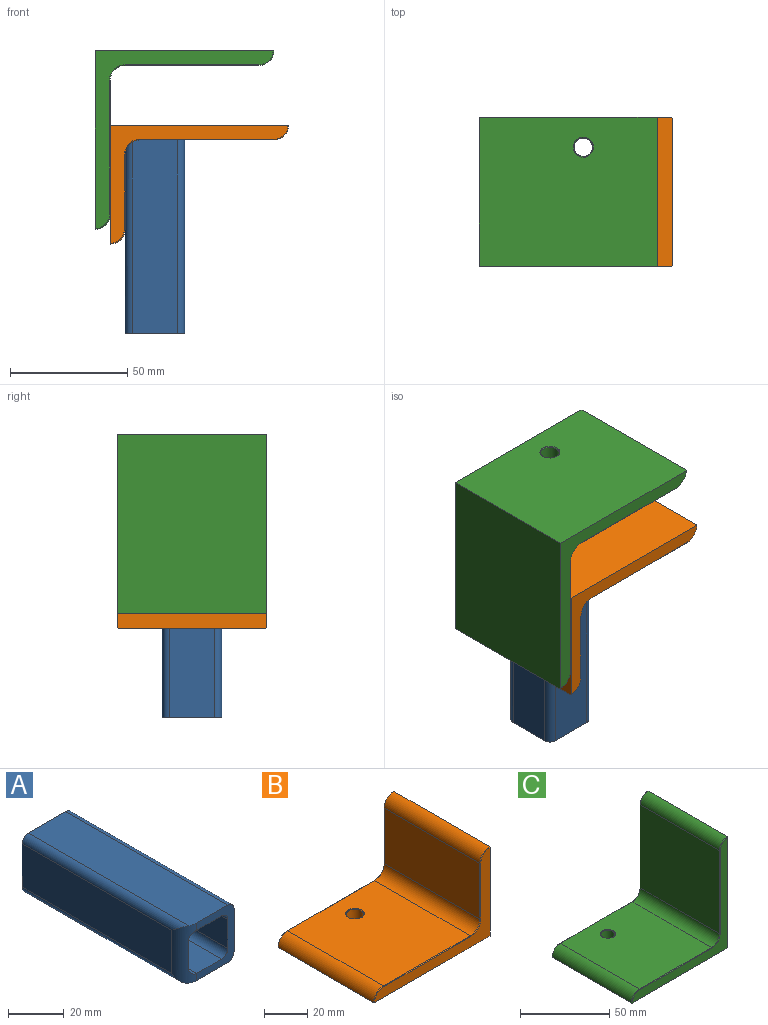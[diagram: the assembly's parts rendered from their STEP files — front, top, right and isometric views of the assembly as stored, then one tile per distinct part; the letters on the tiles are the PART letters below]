
ASSEMBLY  parts=3 mates=2
PART A: 19 faces, bbox 25.4x82.6x25.4 mm
  f0: cylinder r=3.17mm len=82.55mm, axis (0,1,0), area 411.7mm2, adj f1,f15,f16,f17
  f1: plane 82.55x12.7mm, normal (0,0,1), area 1048.4mm2, adj f0,f2,f16,f17
  f2: cylinder r=3.17mm len=82.55mm, axis (0,1,0), area 409.6mm2, adj f1,f3,f17,f18
  f3: plane 81.7x12.7mm, normal (1,0,0), area 1037.6mm2, adj f2,f4,f17,f18
  f4: cylinder r=3.17mm len=82.55mm, axis (0,1,0), area 409.6mm2, adj f3,f5,f17,f18
  f5: plane 82.55x12.7mm, normal (0,0,-1), area 1048.4mm2, adj f4,f6,f16,f17
  f6: cylinder r=3.17mm len=82.55mm, axis (0,1,0), area 411.7mm2, adj f5,f15,f16,f17
  f7: plane 82.55x19.05mm, normal (0,0,-1), area 1571.7mm2, adj f8,f14,f16,f17,f18
  f8: cylinder r=3.17mm len=82.55mm, axis (0,1,0), area 411.7mm2, adj f7,f9,f16,f17
  f9: plane 82.55x19.05mm, normal (1,0,0), area 1572.6mm2, adj f8,f10,f16,f17
  f10: cylinder r=3.17mm len=82.55mm, axis (0,1,0), area 411.7mm2, adj f9,f11,f16,f17
  f11: plane 82.55x19.05mm, normal (0,0,1), area 1571.7mm2, adj f10,f12,f16,f17,f18
  f12: cylinder r=3.17mm len=81.7mm, axis (0,1,0), area 395.6mm2, adj f11,f13,f17,f18
  f13: plane 76.2x19.05mm, normal (-1,0,0), area 1451.6mm2, adj f12,f14,f17,f18
  f14: cylinder r=3.17mm len=81.7mm, axis (0,1,0), area 395.6mm2, adj f7,f13,f17,f18
  f15: plane 82.55x12.7mm, normal (-1,0,0), area 1048.4mm2, adj f0,f6,f16,f17
  f16: plane 25.4x19.05mm, normal (0,-1,0), area 181.5mm2, adj f0,f1,f5,f6,f7,f8,f9,f10
  f17: plane 25.4x25.4mm, normal (0,1,0), area 282.3mm2, adj f0,f1,f2,f3,f4,f5,f6,f7
  f18: cylinder r=6.35mm len=25.4mm, axis (0,0,1), area 178.8mm2, adj f2,f3,f4,f7,f11,f12,f13,f14
PART B: 22 faces, bbox 76.2x63.5x50.8 mm
  f0: cylinder r=6.35mm len=62.87mm, axis (0,1,0), area 627.1mm2, adj f1,f6,f12,f17
  f1: plane 62.87x57.15mm, normal (0,0,1), area 3535mm2, adj f0,f2,f11,f16,f21
  f2: cylinder r=6.35mm len=62.87mm, axis (0,1,0), area 627.1mm2, adj f1,f3,f10,f15
  f3: plane 76.2x63.5mm, normal (0,0,-1), area 4780.9mm2, adj f2,f4,f7,f8,f10,f15,f20
  f4: plane 63.5x50.8mm, normal (1,0,0), area 3225.7mm2, adj f3,f5,f7,f8,f14,f19
  f5: cylinder r=6.35mm len=62.87mm, axis (0,1,0), area 627.1mm2, adj f4,f6,f14,f19
  f6: plane 62.87x31.75mm, normal (-1,0,0), area 1996mm2, adj f0,f5,f13,f18
  f7: plane 75.88x50.48mm, normal (0,-1,0), area 719.8mm2, adj f3,f4,f10,f11,f12,f13,f14
  f8: plane 75.88x50.48mm, normal (0,1,0), area 719.8mm2, adj f3,f4,f15,f16,f17,f18,f19
  f9: cylinder r=3.97mm len=7.94mm, axis (0,0,-1), area 142.5mm2, adj f20,f21
  f10: cone r=6.03mm half-angle=45deg, axis (0,1,0), area 4.4mm2, adj f2,f3,f7,f11
  f11: plane 57.15x0.32mm, normal (0,-0.71,0.71), area 25.7mm2, adj f1,f7,f10,f12
  f12: cone r=6.35mm half-angle=45deg, axis (0,-1,0), area 4.6mm2, adj f0,f7,f11,f13
  f13: plane 31.75x0.32mm, normal (-0.71,-0.71,0), area 14.3mm2, adj f6,f7,f12,f14
  f14: cone r=6.03mm half-angle=45deg, axis (0,1,0), area 4.4mm2, adj f4,f5,f7,f13
  f15: cone r=6.35mm half-angle=45deg, axis (0,-1,0), area 4.4mm2, adj f2,f3,f8,f16
  f16: plane 57.15x0.32mm, normal (0,0.71,0.71), area 25.7mm2, adj f1,f8,f15,f17
  f17: cone r=6.67mm half-angle=45deg, axis (0,1,0), area 4.6mm2, adj f0,f8,f16,f18
  f18: plane 31.75x0.32mm, normal (-0.71,0.71,0), area 14.3mm2, adj f6,f8,f17,f19
  f19: cone r=6.35mm half-angle=45deg, axis (0,-1,0), area 4.4mm2, adj f4,f5,f8,f18
  f20: cone r=3.97mm half-angle=45deg, axis (0,0,-1), area 11.6mm2, adj f3,f9
  f21: cone r=3.97mm half-angle=45deg, axis (0,0,1), area 11.6mm2, adj f1,f9
PART C: 22 faces, bbox 76.2x63.5x76.2 mm
  f0: plane 76.2x63.5mm, normal (1,0,0), area 4838.6mm2, adj f1,f6,f7,f8,f14,f19
  f1: cylinder r=6.35mm len=62.87mm, axis (0,1,0), area 627.1mm2, adj f0,f2,f14,f19
  f2: plane 62.87x57.15mm, normal (-1,0,0), area 3592.7mm2, adj f1,f3,f13,f18
  f3: cylinder r=6.35mm len=62.87mm, axis (0,1,0), area 627.1mm2, adj f2,f4,f12,f17
  f4: plane 62.87x57.15mm, normal (0,0,1), area 3535mm2, adj f3,f5,f11,f16,f21
  f5: cylinder r=6.35mm len=62.87mm, axis (0,1,0), area 627.1mm2, adj f4,f6,f10,f15
  f6: plane 76.2x63.5mm, normal (0,0,-1), area 4780.9mm2, adj f0,f5,f7,f8,f10,f15,f20
  f7: plane 75.88x75.88mm, normal (0,-1,0), area 873.1mm2, adj f0,f6,f10,f11,f12,f13,f14
  f8: plane 75.88x75.88mm, normal (0,1,0), area 873.1mm2, adj f0,f6,f15,f16,f17,f18,f19
  f9: cylinder r=3.97mm len=7.94mm, axis (0,0,-1), area 142.5mm2, adj f20,f21
  f10: cone r=6.03mm half-angle=45deg, axis (0,1,0), area 4.4mm2, adj f5,f6,f7,f11
  f11: plane 57.15x0.32mm, normal (0,-0.71,0.71), area 25.7mm2, adj f4,f7,f10,f12
  f12: cone r=6.35mm half-angle=45deg, axis (0,-1,0), area 4.6mm2, adj f3,f7,f11,f13
  f13: plane 57.15x0.32mm, normal (-0.71,-0.71,0), area 25.7mm2, adj f2,f7,f12,f14
  f14: cone r=6.03mm half-angle=45deg, axis (0,1,0), area 4.4mm2, adj f0,f1,f7,f13
  f15: cone r=6.35mm half-angle=45deg, axis (0,-1,0), area 4.4mm2, adj f5,f6,f8,f16
  f16: plane 57.15x0.32mm, normal (0,0.71,0.71), area 25.7mm2, adj f4,f8,f15,f17
  f17: cone r=6.67mm half-angle=45deg, axis (0,1,0), area 4.6mm2, adj f3,f8,f16,f18
  f18: plane 57.15x0.32mm, normal (-0.71,0.71,0), area 25.7mm2, adj f2,f8,f17,f19
  f19: cone r=6.35mm half-angle=45deg, axis (0,-1,0), area 4.4mm2, adj f0,f1,f8,f18
  f20: cone r=3.97mm half-angle=45deg, axis (0,0,-1), area 11.6mm2, adj f6,f9
  f21: cone r=3.97mm half-angle=45deg, axis (0,0,1), area 11.6mm2, adj f4,f9
PLACE A rot(axis=(-1,0,0),90deg) t=(-6.41,-81.94,-74.7)mm
PLACE B rot(axis=(0,-1,0),180deg) t=(-25.56,-81.94,-27.07)mm
PLACE C rot(axis=(0,-1,0),180deg) t=(-31.81,-81.94,4.68)mm
MATE fastened B.f4 <-> C.f2  axis (-1,0,0) through (-25.46,-81.94,-52.47)mm
MATE fastened A.f13 <-> B.f6  axis (-1,0,0) through (-19.11,-81.94,-39.77)mm
